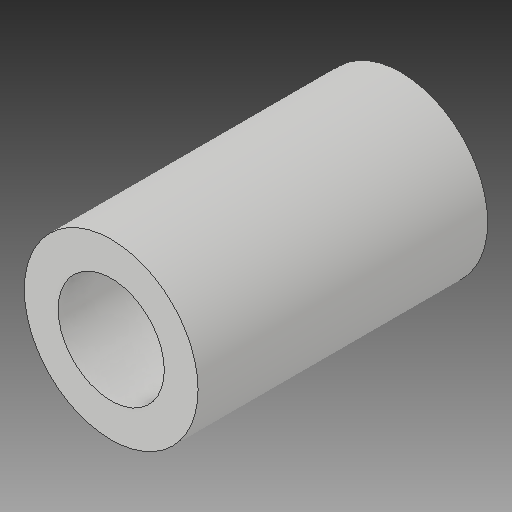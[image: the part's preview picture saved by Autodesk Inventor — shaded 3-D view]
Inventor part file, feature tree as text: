
AUTODESK INVENTOR PART (.ipt)
format: ipt  version: 2017 (Build 210142000, 142)  size: 103,936 bytes
history: native  units: mm
features: other x3, sketch x1
ambient origin geometry x8: Origin, YZ Plane, XZ Plane, XY Plane, X Axis, Y Axis, Z Axis, Center Point
bodies: Solid1 (feature_tree)
feature tree (4):
  other  "Long-Spacer.ipt"
  other  "Solid1::Long-Spacer.ipt"
  other  "TaggingFeature1"
  sketch  "Sketch1"  dims[d0=10.0mm]
